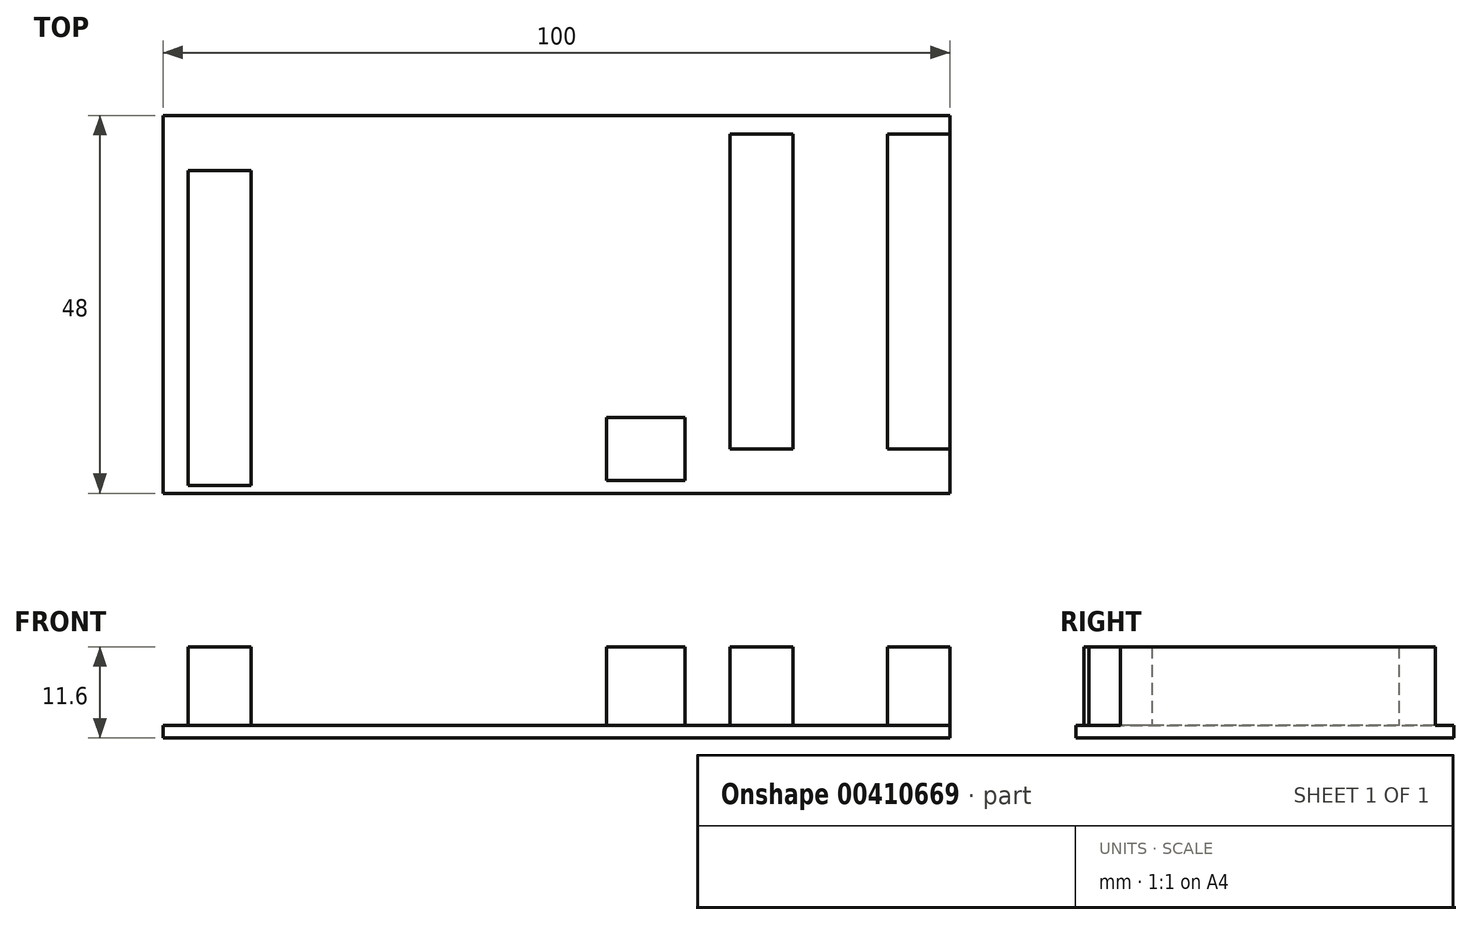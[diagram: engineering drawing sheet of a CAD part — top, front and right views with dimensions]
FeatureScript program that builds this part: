
annotation { "Feature Type Name" : "Feature", "Feature Type Description" : "" }
export const myFeature = defineFeature(function(context is Context, id is Id, definition is map)
    precondition{}
    {
        {
            var Q0;
            Q0=qCreatedBy(makeId("Front.planeOp"),FACE);
            var sketch = newSketch(context, id + "F0", { "sketchPlane" : qUnion([Q0])});
            skLineSegment(sketch, "E0.bottom", {"start": v(50, 0.8) * mm, "end": v(-50, 0.8) * mm});
            skLineSegment(sketch, "E0.top", {"start": v(50, -0.8) * mm, "end": v(-50, -0.8) * mm});
            skLineSegment(sketch, "E0.left", {"start": v(50, 0.8) * mm, "end": v(50, -0.8) * mm});
            skLineSegment(sketch, "E0.right", {"start": v(-50, 0.8) * mm, "end": v(-50, -0.8) * mm});
            skPoint(sketch, "E0.middle", {"position": v(0, 0) * mm});
            skSolve(sketch);
        }
        {
            var Q0;
            Q0 = qSketchRegion(id + "F0", true);
            extrude(context, id + "F1", {"entities" : qUnion([Q0]), "endBound" : BoundingType.SYMMETRIC, "depth" : 48 * mm});
        }
        {
            var Q0;
            Q0=makeQuery(id+"F1.opExtrude","SWEPT_FACE",FACE,{"disambiguationData":[OSD([sQuery(id+"F0.wireOp",EDGE,"E0.bottom")])]});
            var sketch = newSketch(context, id + "F2", { "sketchPlane" : qUnion([Q0])});
            skLineSegment(sketch, "E1.bottom", {"start": v(-46.82, 17) * mm, "end": v(-38.82, 17) * mm});
            skLineSegment(sketch, "E1.top", {"start": v(-46.82, -23) * mm, "end": v(-38.82, -23) * mm});
            skLineSegment(sketch, "E1.left", {"start": v(-46.82, 17) * mm, "end": v(-46.82, -23) * mm});
            skLineSegment(sketch, "E1.right", {"start": v(-38.82, 17) * mm, "end": v(-38.82, -23) * mm});
            skSolve(sketch);
        }
        {
            var Q0;
            Q0 = qSketchRegion(id + "F2", true);
            extrude(context, id + "F3", {"entities" : qUnion([Q0]), "operationType" : NewBodyOperationType.ADD, "depth" : 10 * mm});
        }
        {
            var Q0;
            Q0=makeQuery(id+"F1.opExtrude","SWEPT_FACE",FACE,{"disambiguationData":[OSD([sQuery(id+"F0.wireOp",EDGE,"E0.bottom")])]});
            var sketch = newSketch(context, id + "F4", { "sketchPlane" : qUnion([Q0])});
            skLineSegment(sketch, "E2.bottom", {"start": v(42, 21.6) * mm, "end": v(50, 21.6) * mm});
            skLineSegment(sketch, "E2.top", {"start": v(42, -18.4) * mm, "end": v(50, -18.4) * mm});
            skLineSegment(sketch, "E2.left", {"start": v(42, 21.6) * mm, "end": v(42, -18.4) * mm});
            skLineSegment(sketch, "E2.right", {"start": v(50, 21.6) * mm, "end": v(50, -18.4) * mm});
            skSolve(sketch);
        }
        {
            var Q0;
            Q0 = qSketchRegion(id + "F4", true);
            extrude(context, id + "F5", {"entities" : qUnion([Q0]), "operationType" : NewBodyOperationType.ADD, "depth" : 10 * mm});
        }
        {
            var Q0;
            Q0=makeQuery(id+"F1.opExtrude","SWEPT_FACE",FACE,{"disambiguationData":[OSD([sQuery(id+"F0.wireOp",EDGE,"E0.bottom")])]});
            var sketch = newSketch(context, id + "F6", { "sketchPlane" : qUnion([Q0])});
            skLineSegment(sketch, "E3.bottom", {"start": v(30, 21.63) * mm, "end": v(22, 21.63) * mm});
            skLineSegment(sketch, "E3.top", {"start": v(30, -18.37) * mm, "end": v(22, -18.37) * mm});
            skLineSegment(sketch, "E3.left", {"start": v(30, 21.63) * mm, "end": v(30, -18.37) * mm});
            skLineSegment(sketch, "E3.right", {"start": v(22, 21.63) * mm, "end": v(22, -18.37) * mm});
            skSolve(sketch);
        }
        {
            var Q0;
            Q0 = qSketchRegion(id + "F6", true);
            extrude(context, id + "F7", {"entities" : qUnion([Q0]), "operationType" : NewBodyOperationType.ADD, "depth" : 10 * mm});
        }
        {
            var Q0;
            Q0=makeQuery(id+"F1.opExtrude","SWEPT_FACE",FACE,{"disambiguationData":[OSD([sQuery(id+"F0.wireOp",EDGE,"E0.bottom")])]});
            var sketch = newSketch(context, id + "F8", { "sketchPlane" : qUnion([Q0])});
            skLineSegment(sketch, "E4.bottom", {"start": v(6.32, -14.38) * mm, "end": v(16.32, -14.38) * mm});
            skLineSegment(sketch, "E4.top", {"start": v(6.32, -22.38) * mm, "end": v(16.32, -22.38) * mm});
            skLineSegment(sketch, "E4.left", {"start": v(6.32, -14.38) * mm, "end": v(6.32, -22.38) * mm});
            skLineSegment(sketch, "E4.right", {"start": v(16.32, -14.38) * mm, "end": v(16.32, -22.38) * mm});
            skSolve(sketch);
        }
        {
            var Q0;
            Q0 = qSketchRegion(id + "F8", true);
            extrude(context, id + "F9", {"entities" : qUnion([Q0]), "operationType" : NewBodyOperationType.ADD, "depth" : 10 * mm});
        }
    });
